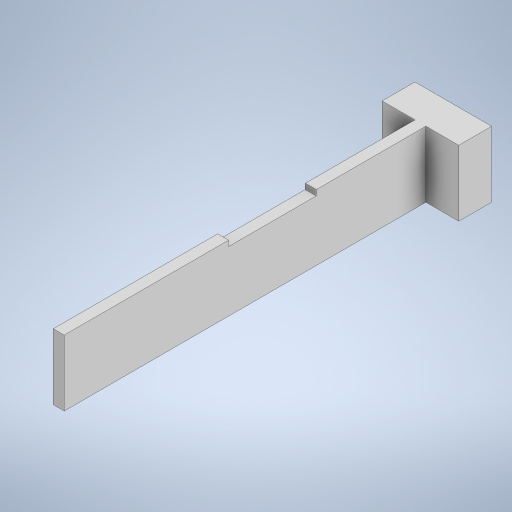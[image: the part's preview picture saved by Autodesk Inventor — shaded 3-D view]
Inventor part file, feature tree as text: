
AUTODESK INVENTOR PART (.ipt)
format: ipt  version: 2024 (Build 280153000, 153)  size: 241,152 bytes
history: native  units: in
note: dims shown in document units (in); Inventor stores cm internally (conversion verified against a paired STEP export)
features: extrude x2, sketch x2
ambient origin geometry x8: Origin, YZ Plane, XZ Plane, XY Plane, X Axis, Y Axis, Z Axis, Center Point
bodies: Solid1 (feature_tree)
feature tree (4):
  extrude  "Extrusion1"  Depth=0.0394in
  extrude  "Extrusion2"  Depth=0.1181in
  sketch  "Sketch1"  dims[d0=1.2992in d1=0.0394in]
  sketch  "Sketch2"  dims[d2=1.2992in d3=0.1181in d4=0.1181in d5=0.2756in d6=0.2362in d7=0.0in d8=0.5906in d9=0.9055in d10=0.0197in d11=0.0in]
